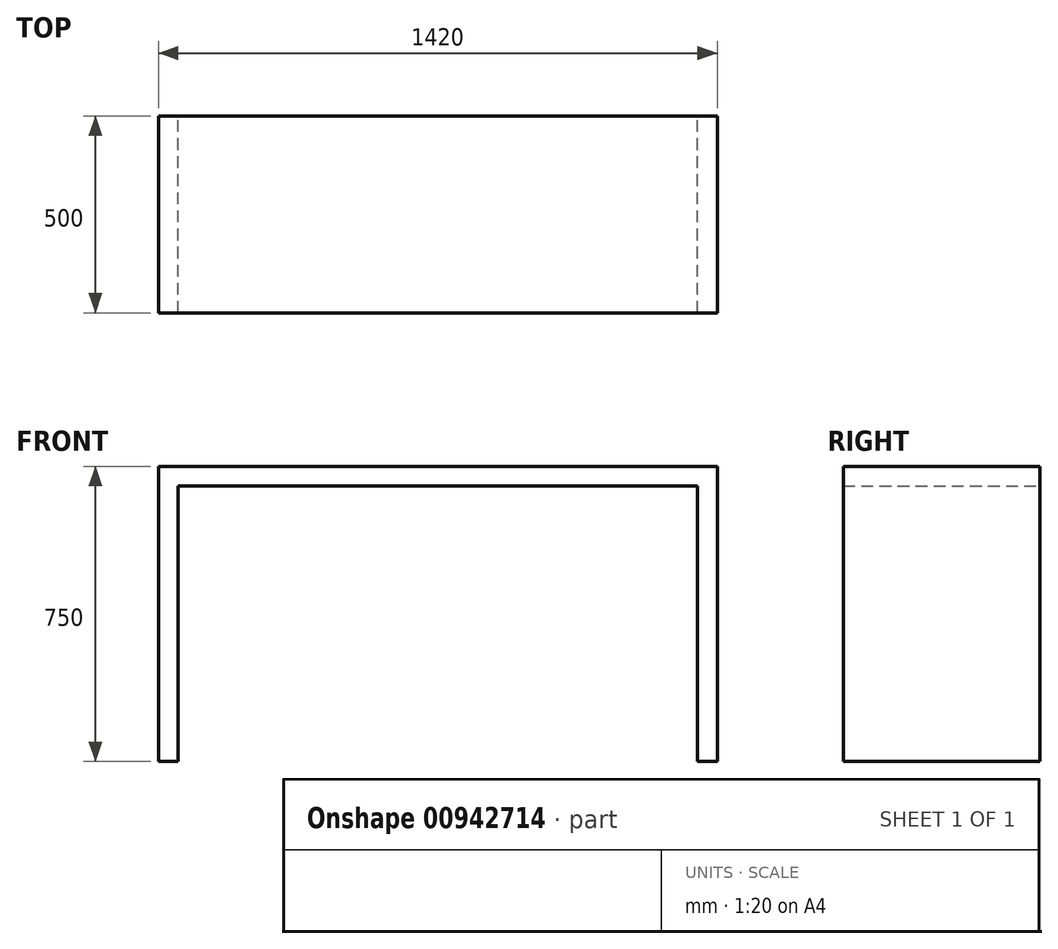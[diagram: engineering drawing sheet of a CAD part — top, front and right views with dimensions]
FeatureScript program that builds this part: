
annotation { "Feature Type Name" : "Feature", "Feature Type Description" : "" }
export const myFeature = defineFeature(function(context is Context, id is Id, definition is map)
    precondition{}
    {
        {
            var Q0;
            Q0=qCreatedBy(makeId("Front.planeOp"),FACE);
            var sketch = newSketch(context, id + "F0", { "sketchPlane" : qUnion([Q0])});
            skLineSegment(sketch, "E0.bottom", {"start": v(-710, -375) * mm, "end": v(710, -375) * mm});
            skLineSegment(sketch, "E0.top", {"start": v(-710, 375) * mm, "end": v(710, 375) * mm});
            skLineSegment(sketch, "E0.left", {"start": v(-710, -375) * mm, "end": v(-710, 375) * mm});
            skLineSegment(sketch, "E0.right", {"start": v(710, -375) * mm, "end": v(710, 375) * mm});
            skLineSegment(sketch, "E1", {"start": v(-710, 0) * mm, "end": v(0, 0) * mm, "construction": true});
            skLineSegment(sketch, "E2", {"start": v(0, 0) * mm, "end": v(710, 0) * mm, "construction": true});
            skLineSegment(sketch, "E3", {"start": v(0, -375) * mm, "end": v(0, 0) * mm, "construction": true});
            skLineSegment(sketch, "E4", {"start": v(0, 0) * mm, "end": v(0, 375) * mm, "construction": true});
            skLineSegment(sketch, "E5", {"start": v(-660, -375) * mm, "end": v(-660, 325) * mm});
            skLineSegment(sketch, "E6", {"start": v(-660, 325) * mm, "end": v(660, 325) * mm});
            skLineSegment(sketch, "E7", {"start": v(660, 325) * mm, "end": v(660, -375) * mm});
            skSolve(sketch);
        }
        {
            var Q0;
            Q0=makeQuery(id+"F0.imprint","IMPRINT",FACE,{"disambiguationData":[TD([[makeQuery(id+"F0.imprint","IMPRINT",EDGE,{"derivedFrom":sQuery(id+"F0.wireOp",EDGE,"E0.top")}),-1.0]])]});
            extrude(context, id + "F1", {"entities" : qUnion([Q0]), "depth" : 500 * mm, "offsetDistance" : 25 * mm});
        }
    });
